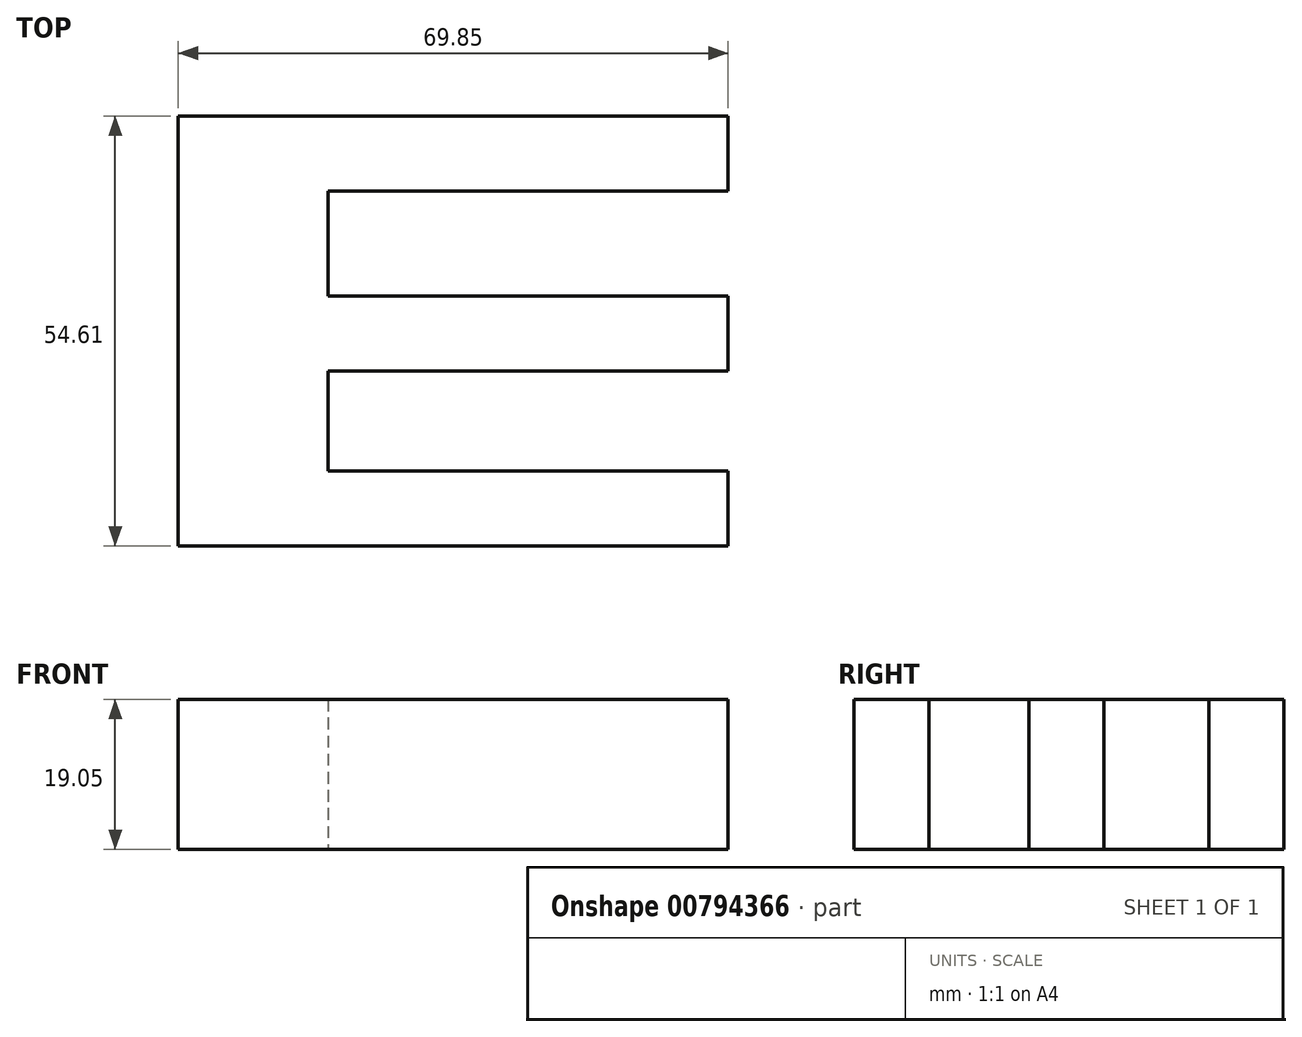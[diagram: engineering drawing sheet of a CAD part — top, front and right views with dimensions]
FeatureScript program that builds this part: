
annotation { "Feature Type Name" : "Feature", "Feature Type Description" : "" }
export const myFeature = defineFeature(function(context is Context, id is Id, definition is map)
    precondition{}
    {
        {
            var Q0;
            Q0=qCreatedBy(makeId("Top.planeOp"),FACE);
            var sketch = newSketch(context, id + "F0", { "sketchPlane" : qUnion([Q0])});
            skLineSegment(sketch, "E0", {"start": v(-30.57, 32.08) * mm, "end": v(-30.57, -22.53) * mm});
            skLineSegment(sketch, "E1", {"start": v(-30.57, -22.53) * mm, "end": v(39.28, -22.53) * mm});
            skLineSegment(sketch, "E2", {"start": v(39.28, -22.53) * mm, "end": v(39.28, -13) * mm});
            skLineSegment(sketch, "E3", {"start": v(39.28, -13) * mm, "end": v(-11.52, -13) * mm});
            skLineSegment(sketch, "E4", {"start": v(-11.52, -13) * mm, "end": v(-11.52, -0.3) * mm});
            skLineSegment(sketch, "E5", {"start": v(-11.52, -0.3) * mm, "end": v(39.28, -0.3) * mm});
            skLineSegment(sketch, "E6", {"start": v(39.28, -0.3) * mm, "end": v(39.28, 9.22) * mm});
            skLineSegment(sketch, "E7", {"start": v(39.28, 9.22) * mm, "end": v(-11.52, 9.22) * mm});
            skLineSegment(sketch, "E8", {"start": v(-11.52, 9.22) * mm, "end": v(-11.52, 22.55) * mm});
            skLineSegment(sketch, "E9", {"start": v(-11.52, 22.55) * mm, "end": v(39.28, 22.55) * mm});
            skLineSegment(sketch, "E10", {"start": v(39.28, 22.55) * mm, "end": v(39.28, 32.08) * mm});
            skLineSegment(sketch, "E11", {"start": v(-30.57, 32.08) * mm, "end": v(39.28, 32.08) * mm});
            skSolve(sketch);
        }
        {
            var Q0;
            Q0=makeQuery(id+"F0.imprint","IMPRINT",FACE,{"disambiguationData":[TD([[makeQuery(id+"F0.imprint","IMPRINT",EDGE,{"derivedFrom":sQuery(id+"F0.wireOp",EDGE,"E0")}),1.0]])]});
            extrude(context, id + "F1", {"entities" : qUnion([Q0]), "depth" : 19.05 * mm, "offsetDistance" : 25.4 * mm});
        }
    });
